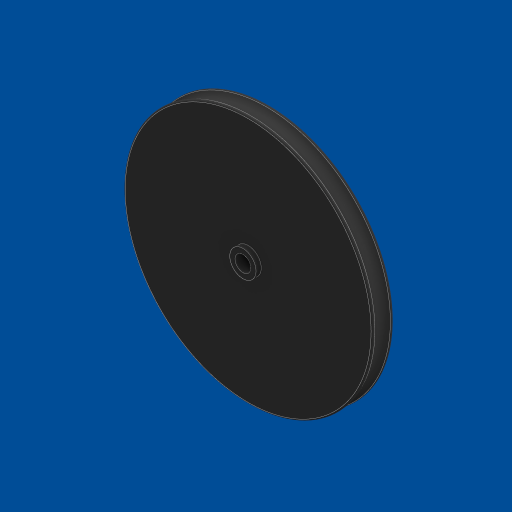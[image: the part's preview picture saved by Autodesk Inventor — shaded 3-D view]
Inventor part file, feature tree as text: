
AUTODESK INVENTOR PART (.ipt)
format: ipt  version: 2023.1 (Build 271208000, 208)  size: 148,992 bytes
history: native  units: mm
features: sketch x3, extrude x3, revolve x1, fillet x1
ambient origin geometry x8: Origin, YZ Plane, XZ Plane, XY Plane, X Axis, Y Axis, Z Axis, Center Point
bodies: Solid1 (feature_tree)
feature tree (8):
  sketch  "Sketch1"  dims[d0=3.0mm d1=50.0mm]
  extrude  "Extrusion1"  Depth=3.0mm
  extrude  "Extrusion2"  Depth=2.0mm TaperAngle=0.0deg
  revolve  "Revolution1"  [1 undecoded]
  fillet  "Fillet1"  [1 undecoded]
  extrude  "Extrusion3"  Depth=0.3mm
  sketch  "Sketch2"  dims[d2=1.0mm d3=2.0mm d4=0.0mm]
  sketch  "Sketch3"  dims[d5=2.0mm d6=0.0mm d7=2.0mm d8=90.0deg d9=0.3mm d10=5.0mm d11=1.0mm d12=0.0mm]
note: 2 required parameter values undecoded (feature->parameter linkage not recoverable at this tier; creation-order binding heuristic only, values carry confidence <= 0.55)